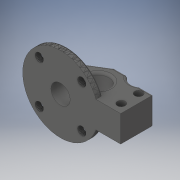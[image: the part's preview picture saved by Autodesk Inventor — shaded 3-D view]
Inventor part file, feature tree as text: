
AUTODESK INVENTOR PART (.ipt)
format: ipt  version: 2018 (Build 220112000, 112)  size: 8,858,112 bytes
history: native  units: mm
features: sketch x12, extrude x10, fillet x6, projected_geometry x4, other x1, imported_body x1
ambient origin geometry x8: Origin, YZ Plane, XZ Plane, XY Plane, X Axis, Y Axis, Z Axis, Center Point
bodies: Volumenkörper1 (feature_tree)
feature tree (34):
  extrude  "Extrusion1"  Depth=10.0mm TaperAngle=0.0deg
  extrude  "Extrusion2"  Depth=22.0mm
  extrude  "Extrusion3"  Depth=10.0mm TaperAngle=0.0deg
  sketch  "Skizze4"  dims[d9=20.5mm d10=0.0mm d11=16.0mm]
  other  "Arbeitsachse1"
  extrude  "Extrusion4"  Depth=16.0mm
  extrude  "Extrusion5"  Depth=18.0mm
  extrude  "Extrusion6"  Depth=16.5mm
  extrude  "Extrusion7"  Depth=10.0mm
  fillet  "Rundung3"  Radius=8.5mm
  fillet  "Rundung4"  Radius=7.0mm
  extrude  "Extrusion8"  Depth=7.5mm
  sketch  "Skizze10"  dims[d33=17.0mm d34=5.0mm d35=10.0mm d36=0.0mm]
  fillet  "Rundung5"  Radius=6.5mm
  extrude  "Extrusion9"  Depth=2.0mm
  fillet  "Rundung7"  Radius=5.0mm
  fillet  "Rundung8"  Radius=19.0mm
  extrude  "Extrusion10"  Depth=10.0mm
  fillet  "Rundung9"  Radius=10.0mm
  sketch  "Skizze1"  dims[d0=20.0mm d1=0.0mm d2=10.0mm d3=0.0mm]
  projected_geometry  "Projizierte Kontur1"
  sketch  "Skizze2"  dims[d4=22.0mm d5=22.0mm]
  projected_geometry  "Projizierte Kontur2"
  sketch  "Skizze3"  dims[d6=67.7mm d7=10.0mm d8=0.0mm]
  projected_geometry  "Projizierte Kontur3"
  sketch  "Skizze5"  dims[d12=22.5mm d13=0.0mm d14=18.0mm]
  projected_geometry  "Projizierte Kontur4"
  sketch  "Skizze6"  dims[d15=35.0mm d17=16.5mm]
  sketch  "Skizze7"  dims[d18=10.0mm d19=0.0mm d20=6.5mm d21=8.5mm d22=7.0mm]
  sketch  "Skizze8"  dims[d23=7.0mm d24=7.5mm d25=6.5mm]
  sketch  "Skizze9"  dims[d26=10.0mm d27=0.0mm d30=2.0mm d31=5.0mm d32=19.0mm]
  sketch  "Skizze11"  dims[d37=2.0mm]
  sketch  "Skizze12"  dims[d38=5.0mm d39=10.0mm d40=0.0mm d42=2.0mm d43=2.0mm d44=3.0mm d45=0.0mm d46=15.0mm d47=2.0mm]
  imported_body  "Basis1"
